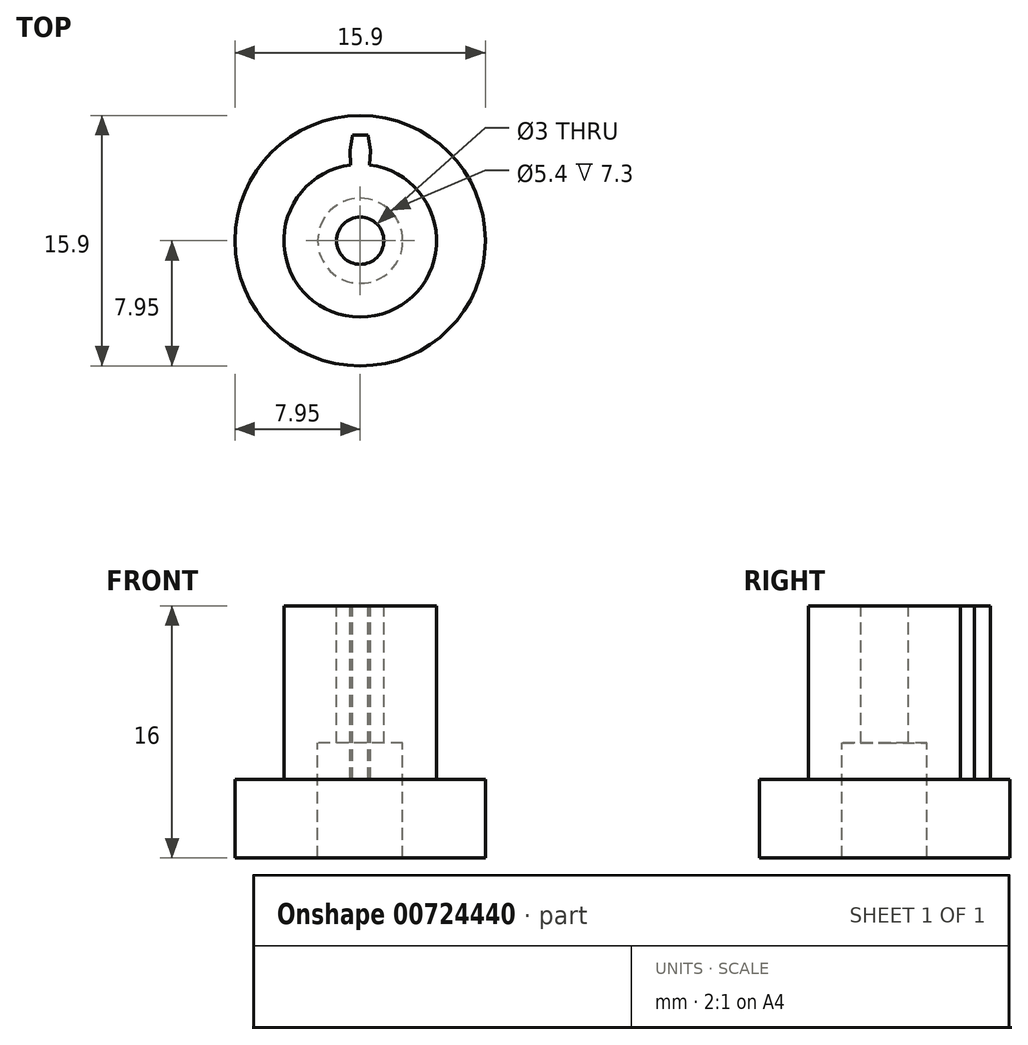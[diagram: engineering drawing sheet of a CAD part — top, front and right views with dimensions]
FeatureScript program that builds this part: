
annotation { "Feature Type Name" : "Feature", "Feature Type Description" : "" }
export const myFeature = defineFeature(function(context is Context, id is Id, definition is map)
    precondition{}
    {
        {
            var Q0;
            Q0=qCreatedBy(makeId("Front.planeOp"),FACE);
            var sketch = newSketch(context, id + "F0", { "sketchPlane" : qUnion([Q0])});
            skLineSegment(sketch, "E0", {"start": v(0, 0) * mm, "end": v(7.95, 0) * mm});
            skLineSegment(sketch, "E1", {"start": v(7.95, 0) * mm, "end": v(7.95, 5) * mm});
            skLineSegment(sketch, "E2", {"start": v(7.95, 5) * mm, "end": v(4.85, 5) * mm});
            skLineSegment(sketch, "E3", {"start": v(4.85, 5) * mm, "end": v(4.85, 16) * mm});
            skLineSegment(sketch, "E4", {"start": v(4.85, 16) * mm, "end": v(0, 16) * mm});
            skLineSegment(sketch, "E5", {"start": v(0, -2.7) * mm, "end": v(0, 22.1) * mm, "construction": true});
            skLineSegment(sketch, "E6", {"start": v(0, 16) * mm, "end": v(0, 0) * mm});
            skSolve(sketch);
        }
        {
            var Q0;
            Q0 = qSketchRegion(id + "F0", true);
            var Q1;
            Q1=sQuery(id+"F0.wireOp",EDGE,"E5");
            revolve(context, id + "F1", {"surfaceOperationType" : NewSurfaceOperationType.NEW, "entities" : qUnion([Q0]), "axis" : qUnion([Q1]), "revolveType" : RevolveType.FULL});
        }
        {
            var Q0;
            Q0=qCreatedBy(makeId("Front.planeOp"),FACE);
            var sketch = newSketch(context, id + "F2", { "sketchPlane" : qUnion([Q0])});
            skLineSegment(sketch, "E7.0", {"start": v(7.95, 0) * mm, "end": v(-7.95, 0) * mm});
            skLineSegment(sketch, "E7.1", {"start": v(4.85, 16) * mm, "end": v(-4.85, 16) * mm});
            skLineSegment(sketch, "E8", {"start": v(0, 0) * mm, "end": v(0, 18.88) * mm, "construction": true});
            skLineSegment(sketch, "E9", {"start": v(1.5, 16) * mm, "end": v(1.5, 7.3) * mm});
            skLineSegment(sketch, "E10", {"start": v(1.5, 7.3) * mm, "end": v(2.7, 7.3) * mm});
            skLineSegment(sketch, "E11", {"start": v(2.7, 7.3) * mm, "end": v(2.7, 0) * mm});
            skLineSegment(sketch, "E12", {"start": v(2.7, 0) * mm, "end": v(0, 0) * mm});
            skLineSegment(sketch, "E13", {"start": v(0, 16) * mm, "end": v(0, 0) * mm});
            skLineSegment(sketch, "E14", {"start": v(0, 16) * mm, "end": v(1.5, 16) * mm});
            skSolve(sketch);
        }
        {
            var Q0;
            Q0 = qSketchRegion(id + "F2", true);
            var Q1;
            Q1=sQuery(id+"F2.wireOp",EDGE,"E8");
            revolve(context, id + "F3", {"operationType" : NewBodyOperationType.REMOVE, "surfaceOperationType" : NewSurfaceOperationType.NEW, "entities" : qUnion([Q0]), "axis" : qUnion([Q1]), "revolveType" : RevolveType.FULL, "oppositeDirection" : true});
        }
        {
            var Q0;
            Q0=makeQuery(id+"F1.opRevolve","SWEPT_FACE",FACE,{"disambiguationData":[OSD([sQuery(id+"F0.wireOp",EDGE,"E4")])]});
            var sketch = newSketch(context, id + "F4", { "sketchPlane" : qUnion([Q0])});
            skLineSegment(sketch, "E15", {"start": v(0, 0) * mm, "end": v(0, 8.27) * mm, "construction": true});
            skLineSegment(sketch, "E16", {"start": v(0, 0) * mm, "end": v(10.63, 0) * mm, "construction": true});
            skLineSegment(sketch, "E17", {"start": v(-0.6, 4.81) * mm, "end": v(-0.65, 5.71) * mm});
            skLineSegment(sketch, "E18", {"start": v(-0.65, 5.71) * mm, "end": v(-0.5, 6.7) * mm});
            skLineSegment(sketch, "E19", {"start": v(-0.5, 6.7) * mm, "end": v(0.5, 6.7) * mm});
            skLineSegment(sketch, "E20", {"start": v(0.5, 6.7) * mm, "end": v(0.65, 5.71) * mm});
            skLineSegment(sketch, "E21", {"start": v(0.65, 5.71) * mm, "end": v(0.6, 4.81) * mm});
            skSolve(sketch);
        }
        {
            var Q0;
            {var subQ0=sQuery(id+"F4.wireOp",EDGE,"E17");Q0=makeQuery(id+"F4.imprint","IMPRINT",FACE,{"disambiguationData":[TD([[makeQuery(id+"F4.imprint","IMPRINT",EDGE,{"derivedFrom":subQ0}),-1.0]])]});}
            extrude(context, id + "F5", {"entities" : qUnion([Q0]), "operationType" : NewBodyOperationType.ADD, "endBound" : BoundingType.UP_TO_NEXT, "oppositeDirection" : true, "depth" : 25 * mm, "offsetDistance" : 25 * mm});
        }
    });
